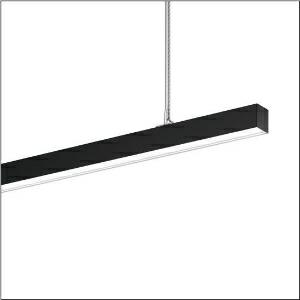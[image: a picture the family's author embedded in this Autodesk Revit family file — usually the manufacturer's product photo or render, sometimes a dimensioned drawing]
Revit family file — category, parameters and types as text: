
# Revit family: silica_r__21_51mx30da34bb_31c6
name_source: partatom
category: Lighting Fixtures
units: mm (PartAtom-declared; Revit-internal decimal feet)

## family parameters
Cut with Voids When Loaded = No
Host = Face
Light Source = No
Part Type = Normal
Room Calculation Point = No
Round Connector Dimension = Use Diameter
Shared = No

## types (1)
- --- (1 x LED, 4210 lm, 27.7 W, 3000K)
    Apparent Load = 28 VA
    CIE Flux Codes = 47 79 96 57 100
    Color Rendering = 80
    Color Temperature = 3000K
    Default Elevation = 1800 mm
    Description = Silica® 21, office luminaire, primary optical cover: cover, of PMMA, opal, light emission: direct/indirect distribution, primary light characteristic: symmetric, installation type: suspended mounting, LED, rated luminous flux: 4.210lm, luminous efficacy: 152lm/W, light colour: 830, colour temperature: 3000K, control gear: DALI 2, with terminal, 3+2-pole, max. 2.5mm², mains connection: 220..240V, AC, 50/60Hz, rated input power: 27.7W, luminaire housing, of aluminium, matt jet black (RAL 9005), length: 1.204mm, width: 53mm, height: 53mm, protection rating (complete): IP20, insulation class (complete): insulation class I (protective earthing), certification: CE, permissible operating ambient temperature: 0..+35°C, standard: EN 50419, packaging unit: 1 piece
    Height = 53 mm
    Lamp = 1 x LED
    Lamp Light Flux = 4210 lm
    Lamp Power = 27.7 W
    Lamp count = 1
    Length = 1204 mm
    Luminous efficacy = 152 lm/W
    Manufacturer = Siteco
    ModVariant = No
    Model = 51MX30DA34BB
    Mounting Place = Ceiling
    Mounting Type = Pendant
    Number of Poles = 1
    OnlyDefault = Yes
    Power Factor = 1
    Product Name = Silica® 21
    Product group = office luminaire | ceiling pendant
    ProductGroupID = 904
    Protection Class = Protection class I
    Protection Degree = IP 20
    RLX_Detail_Level = 1
    RLX_Emergency_Light_Flux = 0 lm
    RLX_Emergency_Type = 0
    RLX_Emergency_Type_DB = No
    RlxData = <blob elided: 26057 chars, md5=3eef95d8>
    Socket = socket
    Standby Power = 0 W
    System Light Flux = 4210 lm
    System Power = 28 W
    Type Comments = factory setting: luminous flux: 100 % | dim-lin: 254 | 233 mA
    Type Image = l_1335856.jpg
    URL = http://relux.com
    VarID = @adj_117310
    Voltage = 0 V
    Weight = 0.00 kg
    Width = 53 mm

## geometry (parser evidence)
native form markers: Blend x4, Sweep x13
no freeform markers — native parametric forms only
